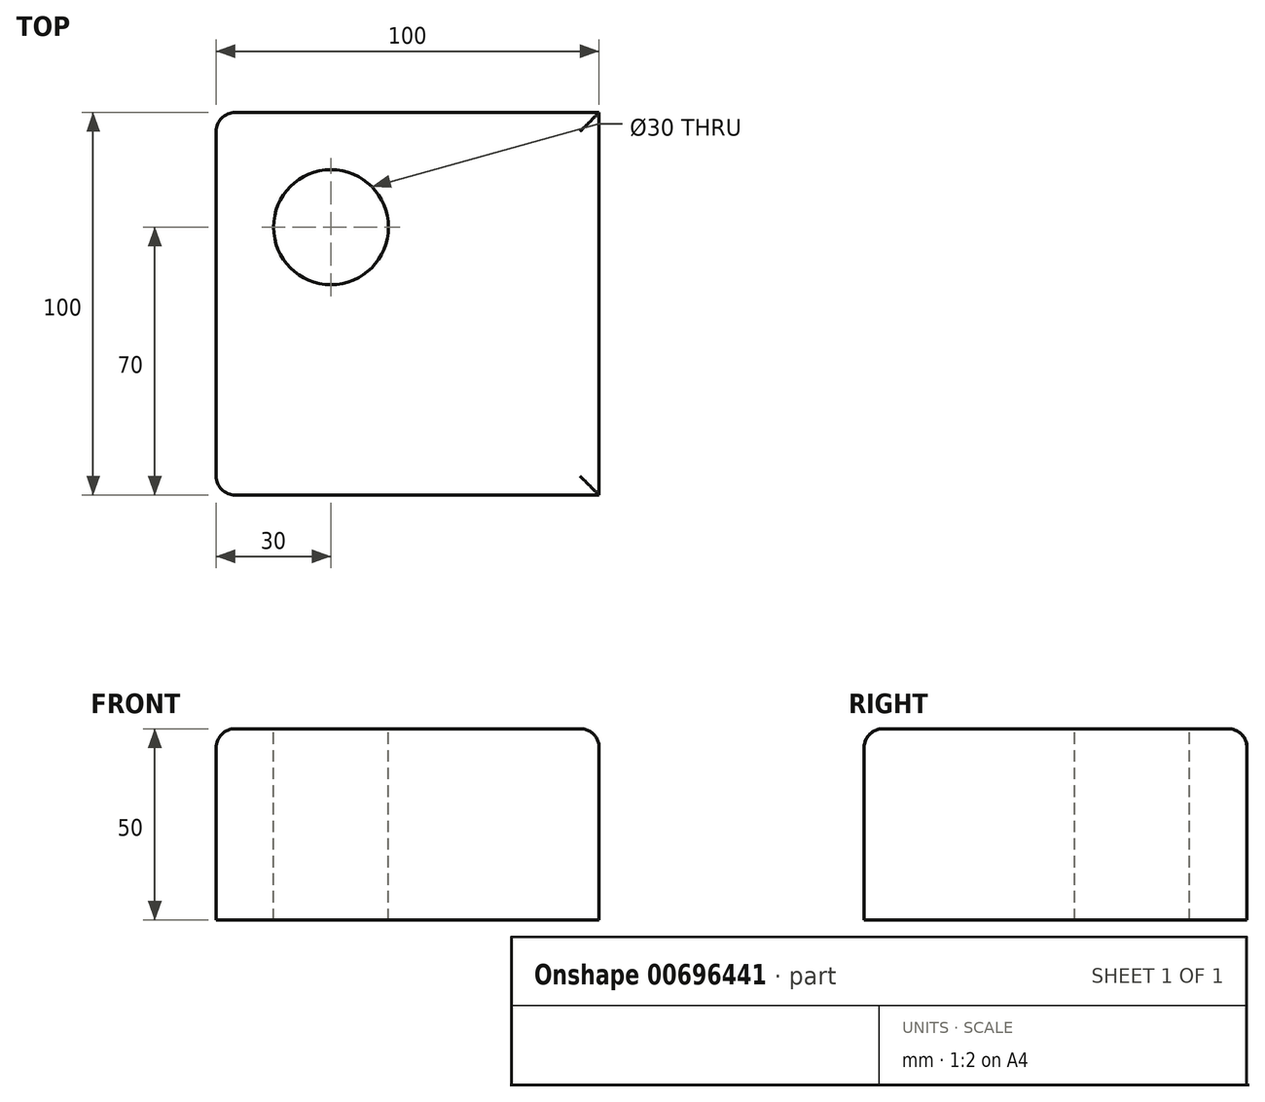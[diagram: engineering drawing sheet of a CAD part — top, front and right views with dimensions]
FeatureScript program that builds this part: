
annotation { "Feature Type Name" : "Feature", "Feature Type Description" : "" }
export const myFeature = defineFeature(function(context is Context, id is Id, definition is map)
    precondition{}
    {
        {
            var Q0;
            Q0=qCreatedBy(makeId("Top.planeOp"),FACE);
            var sketch = newSketch(context, id + "F0", { "sketchPlane" : qUnion([Q0])});
            skLineSegment(sketch, "E0.bottom", {"start": v(-50, 50) * mm, "end": v(50, 50) * mm});
            skLineSegment(sketch, "E0.top", {"start": v(-50, -50) * mm, "end": v(50, -50) * mm});
            skLineSegment(sketch, "E0.left", {"start": v(-50, 50) * mm, "end": v(-50, -50) * mm});
            skLineSegment(sketch, "E0.right", {"start": v(50, 50) * mm, "end": v(50, -50) * mm});
            skSolve(sketch);
        }
        {
            var Q0;
            Q0 = qSketchRegion(id + "F0", true);
            extrude(context, id + "F1", {"entities" : qUnion([Q0]), "depth" : 50 * mm, "offsetDistance" : 25 * mm});
        }
        {
            var Q0;
            Q0=makeQuery(id+"F1.opExtrude","CAP_FACE",FACE,{"disambiguationData":[OSD([sQuery(id+"F0.wireOp",EDGE,"E0.bottom"),sQuery(id+"F0.wireOp",EDGE,"E0.top"),sQuery(id+"F0.wireOp",EDGE,"E0.left"),sQuery(id+"F0.wireOp",EDGE,"E0.right")])],"isStart":false});
            var sketch = newSketch(context, id + "F2", { "sketchPlane" : qUnion([Q0])});
            skCircle(sketch, "E1", {"center": v(-20, 20) * mm, "radius": 15 * mm});
            skSolve(sketch);
        }
        {
            var Q0;
            Q0 = qSketchRegion(id + "F2", true);
            extrude(context, id + "F3", {"entities" : qUnion([Q0]), "operationType" : NewBodyOperationType.REMOVE, "endBound" : BoundingType.THROUGH_ALL, "oppositeDirection" : true, "depth" : 25 * mm, "offsetDistance" : 25 * mm});
        }
        {
            var Q0;
            Q0=makeQuery(id+"F1.opExtrude","CAP_EDGE",EDGE,{"disambiguationData":[OSD([sQuery(id+"F0.wireOp",EDGE,"E0.left")])],"isStart":false});
            fillet(context, id + "F4", {"entities" : qUnion([Q0]), "radius" : 5 * mm, "tangentPropagation" : true, "allowEdgeOverflow" : false});
        }
        {
            var Q0;
            Q0=makeQuery(id+"F1.opExtrude","CAP_EDGE",EDGE,{"disambiguationData":[OSD([sQuery(id+"F0.wireOp",EDGE,"E0.top")])],"isStart":false});
            var Q1;
            Q1=makeQuery(id+"F1.opExtrude","CAP_EDGE",EDGE,{"disambiguationData":[OSD([sQuery(id+"F0.wireOp",EDGE,"E0.right")])],"isStart":false});
            var Q2;
            Q2=makeQuery(id+"F1.opExtrude","CAP_EDGE",EDGE,{"disambiguationData":[OSD([sQuery(id+"F0.wireOp",EDGE,"E0.bottom")])],"isStart":false});
            fillet(context, id + "F5", {"entities" : qUnion([Q0, Q1, Q2]), "radius" : 5 * mm, "tangentPropagation" : true, "allowEdgeOverflow" : false});
        }
    });
